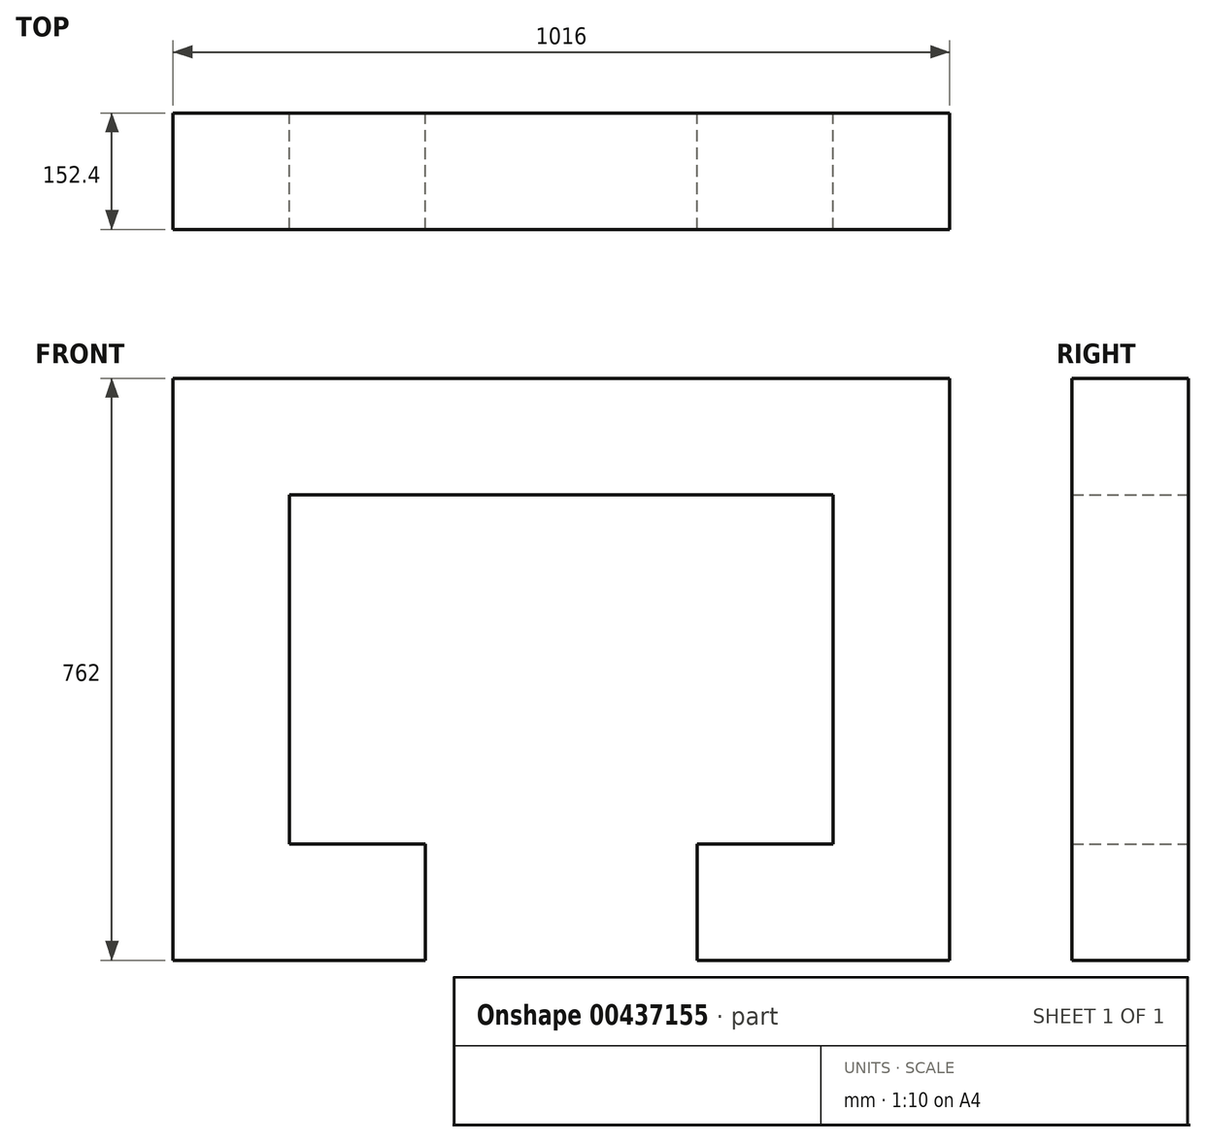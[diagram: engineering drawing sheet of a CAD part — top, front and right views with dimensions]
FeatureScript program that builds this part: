
annotation { "Feature Type Name" : "Feature", "Feature Type Description" : "" }
export const myFeature = defineFeature(function(context is Context, id is Id, definition is map)
    precondition{}
    {
        {
            var Q0;
            Q0=qCreatedBy(makeId("Front.planeOp"),FACE);
            var sketch = newSketch(context, id + "F0", { "sketchPlane" : qUnion([Q0])});
            skLineSegment(sketch, "E0.bottom", {"start": v(0, 0) * mm, "end": v(-1016, 0) * mm});
            skLineSegment(sketch, "E0.top", {"start": v(0, 152.4) * mm, "end": v(-1016, 152.4) * mm});
            skLineSegment(sketch, "E0.left", {"start": v(0, 0) * mm, "end": v(0, 152.4) * mm});
            skLineSegment(sketch, "E0.right", {"start": v(-1016, 0) * mm, "end": v(-1016, 152.4) * mm});
            skLineSegment(sketch, "E1.bottom", {"start": v(-1016, 0) * mm, "end": v(-863.6, 0) * mm});
            skLineSegment(sketch, "E1.top", {"start": v(-1016, -457.2) * mm, "end": v(-863.6, -457.2) * mm});
            skLineSegment(sketch, "E1.left", {"start": v(-1016, 0) * mm, "end": v(-1016, -457.2) * mm});
            skLineSegment(sketch, "E1.right", {"start": v(-863.6, 0) * mm, "end": v(-863.6, -457.2) * mm});
            skLineSegment(sketch, "E2.bottom", {"start": v(-1016, -457.2) * mm, "end": v(-685.8, -457.2) * mm});
            skLineSegment(sketch, "E2.top", {"start": v(-1016, -609.6) * mm, "end": v(-685.8, -609.6) * mm});
            skLineSegment(sketch, "E2.left", {"start": v(-1016, -457.2) * mm, "end": v(-1016, -609.6) * mm});
            skLineSegment(sketch, "E2.right", {"start": v(-685.8, -457.2) * mm, "end": v(-685.8, -609.6) * mm});
            skLineSegment(sketch, "E3.bottom", {"start": v(0, 0) * mm, "end": v(-152.4, 0) * mm});
            skLineSegment(sketch, "E3.top", {"start": v(0, -457.2) * mm, "end": v(-152.4, -457.2) * mm});
            skLineSegment(sketch, "E3.left", {"start": v(0, 0) * mm, "end": v(0, -457.2) * mm});
            skLineSegment(sketch, "E3.right", {"start": v(-152.4, 0) * mm, "end": v(-152.4, -457.2) * mm});
            skLineSegment(sketch, "E4.bottom", {"start": v(0, -457.2) * mm, "end": v(-330.2, -457.2) * mm});
            skLineSegment(sketch, "E4.top", {"start": v(0, -609.6) * mm, "end": v(-330.2, -609.6) * mm});
            skLineSegment(sketch, "E4.left", {"start": v(0, -457.2) * mm, "end": v(0, -609.6) * mm});
            skLineSegment(sketch, "E4.right", {"start": v(-330.2, -457.2) * mm, "end": v(-330.2, -609.6) * mm});
            skSolve(sketch);
        }
        {
            var Q0;
            Q0 = qSketchRegion(id + "F0", true);
            extrude(context, id + "F1", {"entities" : qUnion([Q0]), "depth" : 152.4 * mm});
        }
    });
